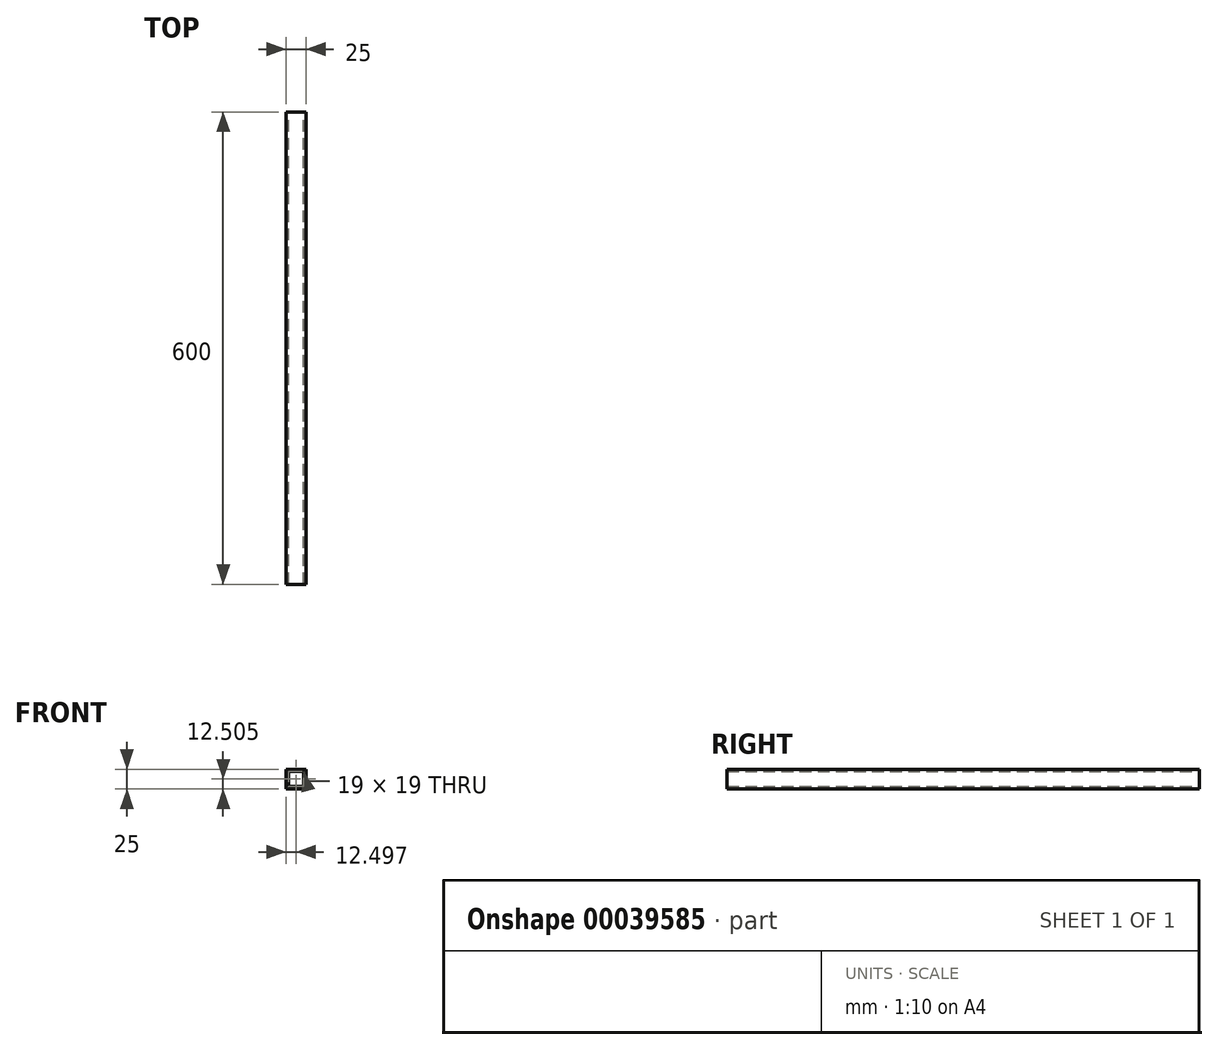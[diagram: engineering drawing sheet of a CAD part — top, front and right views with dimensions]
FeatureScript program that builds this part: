
annotation { "Feature Type Name" : "Feature", "Feature Type Description" : "" }
export const myFeature = defineFeature(function(context is Context, id is Id, definition is map)
    precondition{}
    {
        {
            var Q0;
            Q0=qCreatedBy(makeId("Front.planeOp"),FACE);
            var sketch = newSketch(context, id + "F0", { "sketchPlane" : qUnion([Q0])});
            skLineSegment(sketch, "E0.bottom", {"start": v(-57.78, 50.37) * mm, "end": v(-32.78, 50.37) * mm});
            skLineSegment(sketch, "E0.top", {"start": v(-57.78, 25.37) * mm, "end": v(-32.78, 25.37) * mm});
            skLineSegment(sketch, "E0.left", {"start": v(-57.78, 50.37) * mm, "end": v(-57.78, 25.37) * mm});
            skLineSegment(sketch, "E0.right", {"start": v(-32.78, 50.37) * mm, "end": v(-32.78, 25.37) * mm});
            skLineSegment(sketch, "E1.bottom", {"start": v(-54.78, 47.37) * mm, "end": v(-35.78, 47.37) * mm});
            skLineSegment(sketch, "E1.top", {"start": v(-54.78, 28.37) * mm, "end": v(-35.78, 28.37) * mm});
            skLineSegment(sketch, "E1.left", {"start": v(-54.78, 47.37) * mm, "end": v(-54.78, 28.37) * mm});
            skLineSegment(sketch, "E1.right", {"start": v(-35.78, 47.37) * mm, "end": v(-35.78, 28.37) * mm});
            skSolve(sketch);
        }
        {
            var Q0;
            Q0=qSketchRegion(id+"F0",true);
            extrude(context, id + "F1", {"entities" : qUnion([Q0]), "depth" : 600 * mm});
        }
    });
